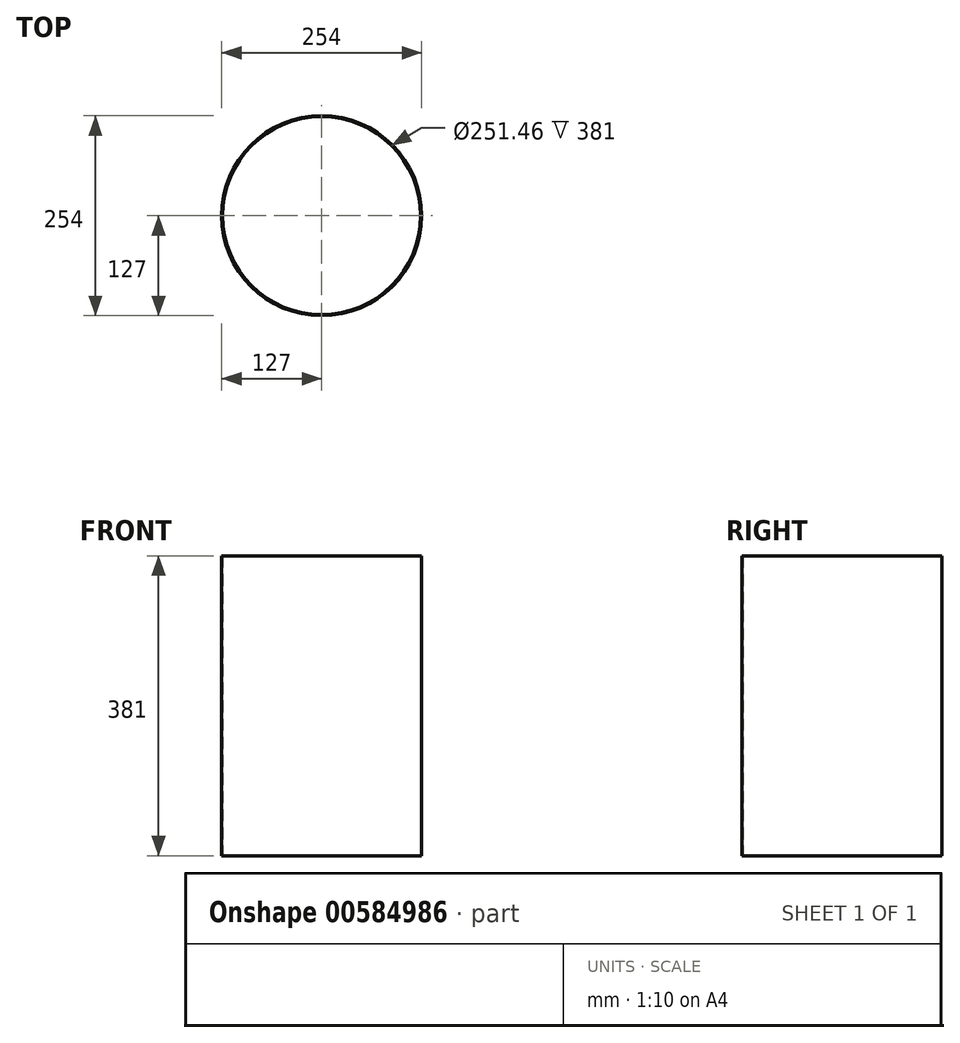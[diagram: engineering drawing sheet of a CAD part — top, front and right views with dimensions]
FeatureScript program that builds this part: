
annotation { "Feature Type Name" : "Feature", "Feature Type Description" : "" }
export const myFeature = defineFeature(function(context is Context, id is Id, definition is map)
    precondition{}
    {
        {
            var Q0;
            Q0=qCreatedBy(makeId("Top.planeOp"),FACE);
            var sketch = newSketch(context, id + "F0", { "sketchPlane" : qUnion([Q0])});
            skCircle(sketch, "E0", {"center": v(0, 0) * mm, "radius": 127 * mm});
            skCircle(sketch, "E1", {"center": v(0, 0) * mm, "radius": 125.73 * mm});
            skSolve(sketch);
        }
        {
            var Q0;
            Q0=makeQuery(id+"F0.imprint","IMPRINT",FACE,{"disambiguationData":[TD([[makeQuery(id+"F0.imprint","IMPRINT",EDGE,{"derivedFrom":sQuery(id+"F0.wireOp",EDGE,"E0")}),1.0]])]});
            extrude(context, id + "F1", {"entities" : qUnion([Q0]), "depth" : 381 * mm, "offsetDistance" : 25.4 * mm});
        }
    });
